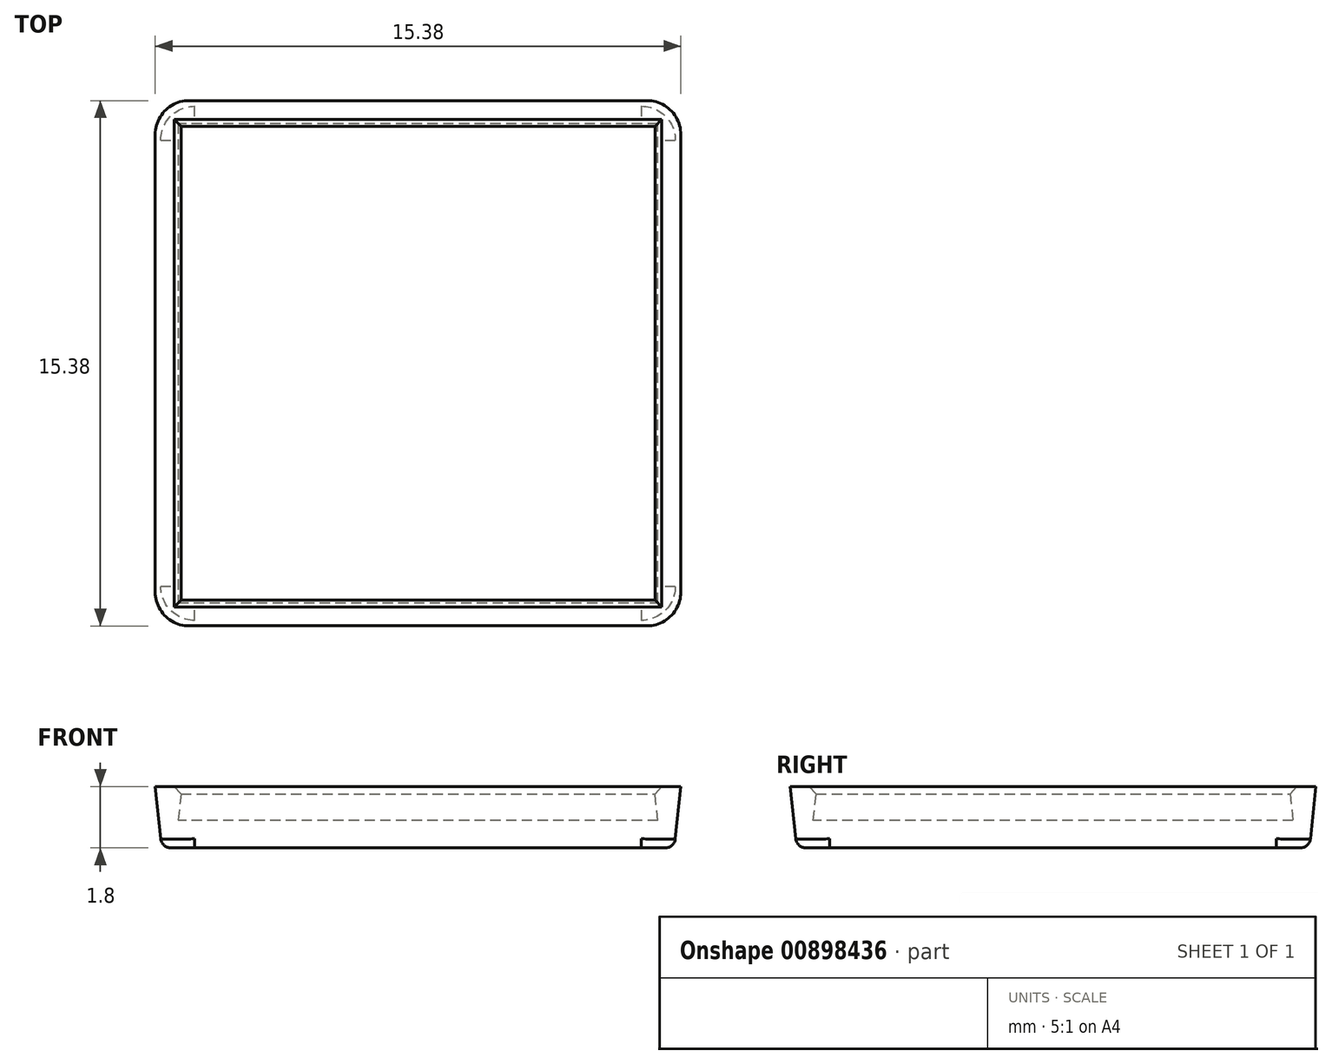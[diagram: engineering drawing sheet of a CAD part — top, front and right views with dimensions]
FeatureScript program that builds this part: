
annotation { "Feature Type Name" : "Feature", "Feature Type Description" : "" }
export const myFeature = defineFeature(function(context is Context, id is Id, definition is map)
    precondition{}
    {
        {
            var Q0;
            Q0=qCreatedBy(makeId("Top.planeOp"),FACE);
            var sketch = newSketch(context, id + "F0", { "sketchPlane" : qUnion([Q0])});
            skLineSegment(sketch, "E0.bottom", {"start": v(0, 0) * mm, "end": v(15, 0) * mm});
            skLineSegment(sketch, "E0.top", {"start": v(0, 15) * mm, "end": v(15, 15) * mm});
            skLineSegment(sketch, "E0.left", {"start": v(0, 0) * mm, "end": v(0, 15) * mm});
            skLineSegment(sketch, "E0.right", {"start": v(15, 0) * mm, "end": v(15, 15) * mm});
            skLineSegment(sketch, "E1.0", {"start": v(0.4, 14.6) * mm, "end": v(14.6, 14.6) * mm});
            skLineSegment(sketch, "E1.1", {"start": v(0.4, 0.4) * mm, "end": v(0.4, 14.6) * mm});
            skLineSegment(sketch, "E1.2", {"start": v(0.4, 0.4) * mm, "end": v(14.6, 0.4) * mm});
            skLineSegment(sketch, "E1.3", {"start": v(14.6, 0.4) * mm, "end": v(14.6, 14.6) * mm});
            skSolve(sketch);
        }
        {
            var Q0;
            Q0=makeQuery(id+"F0.imprint","IMPRINT",FACE,{"disambiguationData":[TD([[makeQuery(id+"F0.imprint","IMPRINT",EDGE,{"derivedFrom":sQuery(id+"F0.wireOp",EDGE,"E0.bottom")}),1.0]])]});
            extrude(context, id + "F1", {"entities" : qUnion([Q0]), "depth" : 1.8 * mm, "offsetDistance" : 25 * mm, "hasDraft" : true, "draftAngle" : 6 * degree});
        }
        {
            var Q0;
            Q0=makeQuery(id+"F0.imprint","IMPRINT",FACE,{"disambiguationData":[TD([[makeQuery(id+"F0.imprint","IMPRINT",EDGE,{"derivedFrom":sQuery(id+"F0.wireOp",EDGE,"E1.0")}),-1.0]])]});
            extrude(context, id + "F2", {"entities" : qUnion([Q0]), "operationType" : NewBodyOperationType.ADD, "depth" : 0.8 * mm, "offsetDistance" : 25 * mm});
        }
        {
            var Q0;
            {var subQ0=sQuery(id+"F0.wireOp",EDGE,"E1.3");var subQ1=sQuery(id+"F0.wireOp",EDGE,"E1.2");var subQ2=sQuery(id+"F0.wireOp",EDGE,"E1.1");var subQ3=sQuery(id+"F0.wireOp",EDGE,"E1.0");Q0=makeQuery(id+"F2.boolean.opBoolean","MERGE",FACE,{"derivedFrom":[makeQuery(id+"F1.opExtrude","CAP_FACE",FACE,{"disambiguationData":[OSD([sQuery(id+"F0.wireOp",EDGE,"E0.bottom"),sQuery(id+"F0.wireOp",EDGE,"E0.top"),sQuery(id+"F0.wireOp",EDGE,"E0.left"),sQuery(id+"F0.wireOp",EDGE,"E0.right"),subQ3,subQ2,subQ1,subQ0])],"isStart":true}),makeQuery(id+"F2.opExtrude","CAP_FACE",FACE,{"disambiguationData":[OSD([subQ3,subQ2,subQ1,subQ0])],"isStart":true})]});}
            fillet(context, id + "F3", {"entities" : qUnion([Q0]), "radius" : .3 * mm, "tangentPropagation" : true, "allowEdgeOverflow" : false});
        }
        {
            var Q0;
            Q0=makeQuery(id+"F1.opExtrude","SWEPT_EDGE",EDGE,{"disambiguationData":[OSD([sQuery(id+"F0.wireOp",EDGE,"E0.top"),sQuery(id+"F0.wireOp",EDGE,"E0.left")])]});
            var Q1;
            Q1=makeQuery(id+"F1.opExtrude","SWEPT_EDGE",EDGE,{"disambiguationData":[OSD([sQuery(id+"F0.wireOp",EDGE,"E0.bottom"),sQuery(id+"F0.wireOp",EDGE,"E0.left")])]});
            var Q2;
            Q2=makeQuery(id+"F1.opExtrude","SWEPT_EDGE",EDGE,{"disambiguationData":[OSD([sQuery(id+"F0.wireOp",EDGE,"E0.bottom"),sQuery(id+"F0.wireOp",EDGE,"E0.right")])]});
            var Q3;
            Q3=makeQuery(id+"F1.opExtrude","SWEPT_EDGE",EDGE,{"disambiguationData":[OSD([sQuery(id+"F0.wireOp",EDGE,"E0.top"),sQuery(id+"F0.wireOp",EDGE,"E0.right")])]});
            fillet(context, id + "F4", {"entities" : qUnion([Q0, Q1, Q2, Q3]), "radius" : 1 * mm, "tangentPropagation" : true, "allowEdgeOverflow" : false});
        }
        {
            var Q0;
            Q0=makeQuery(id+"F1.opExtrude","CAP_EDGE",EDGE,{"disambiguationData":[OSD([sQuery(id+"F0.wireOp",EDGE,"E1.0")])],"isStart":false});
            var Q1;
            Q1=makeQuery(id+"F1.opExtrude","CAP_EDGE",EDGE,{"disambiguationData":[OSD([sQuery(id+"F0.wireOp",EDGE,"E1.1")])],"isStart":false});
            var Q2;
            Q2=makeQuery(id+"F1.opExtrude","CAP_EDGE",EDGE,{"disambiguationData":[OSD([sQuery(id+"F0.wireOp",EDGE,"E1.2")])],"isStart":false});
            var Q3;
            Q3=makeQuery(id+"F1.opExtrude","CAP_EDGE",EDGE,{"disambiguationData":[OSD([sQuery(id+"F0.wireOp",EDGE,"E1.3")])],"isStart":false});
            chamfer(context, id + "F5", {"entities" : qUnion([Q0, Q1, Q2, Q3]), "width" : .2 * mm, "tangentPropagation" : true});
        }
    });
